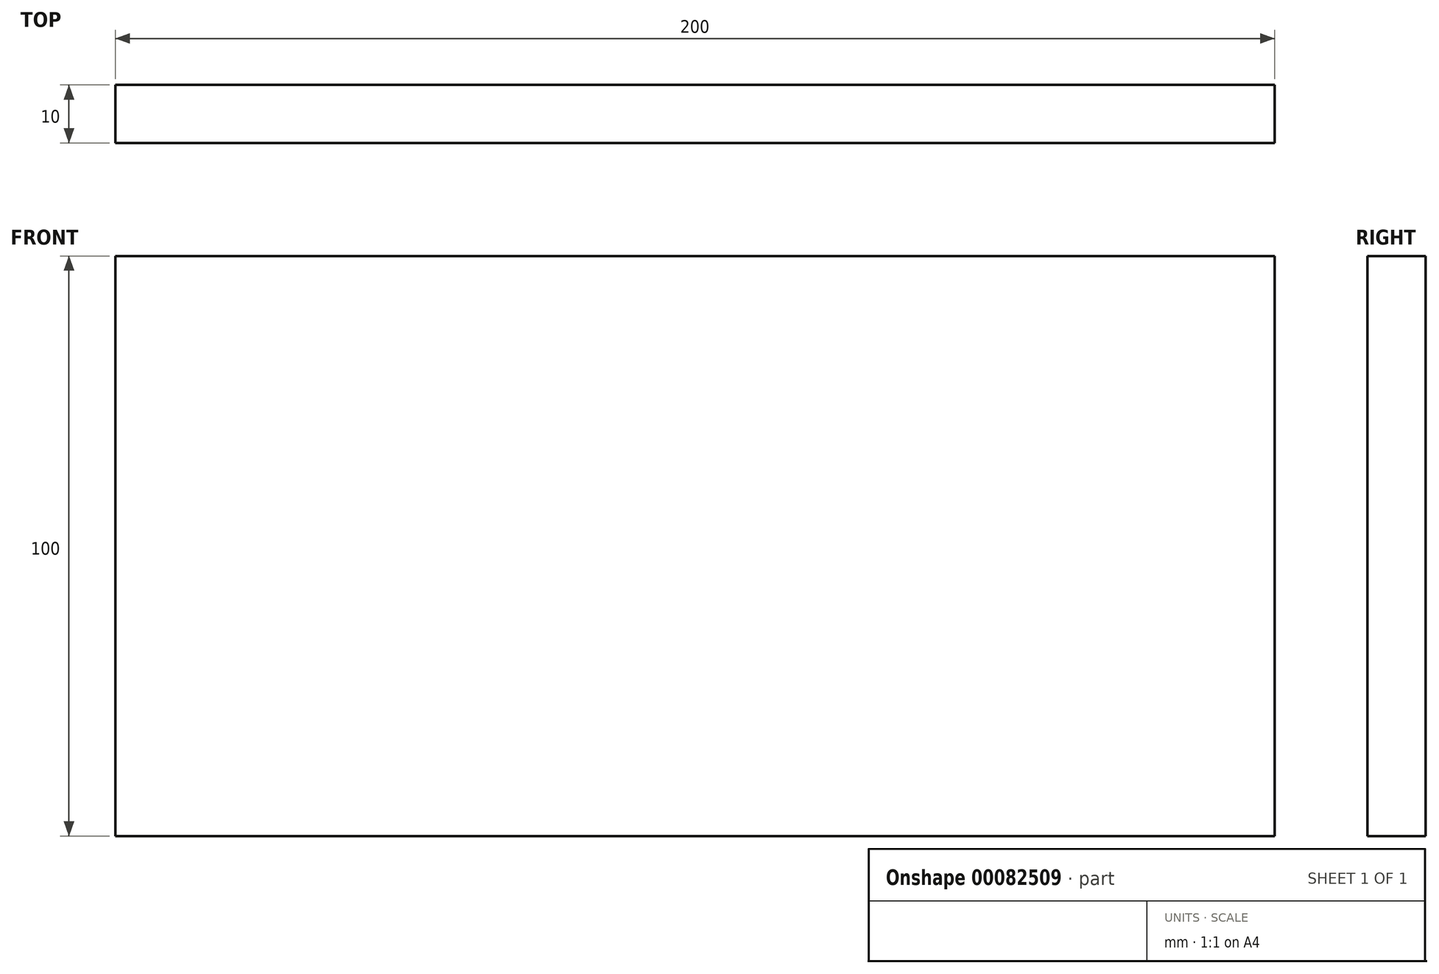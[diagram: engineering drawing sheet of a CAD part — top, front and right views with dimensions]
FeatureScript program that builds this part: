
annotation { "Feature Type Name" : "Feature", "Feature Type Description" : "" }
export const myFeature = defineFeature(function(context is Context, id is Id, definition is map)
    precondition{}
    {
        {
            var Q0;
            Q0=qCreatedBy(makeId("Front.planeOp"),FACE);
            var sketch = newSketch(context, id + "F0", { "sketchPlane" : qUnion([Q0])});
            skLineSegment(sketch, "E0.bottom", {"start": v(0, 0) * mm, "end": v(-200, 0) * mm});
            skLineSegment(sketch, "E0.top", {"start": v(0, 100) * mm, "end": v(-200, 100) * mm});
            skLineSegment(sketch, "E0.left", {"start": v(0, 0) * mm, "end": v(0, 100) * mm});
            skLineSegment(sketch, "E0.right", {"start": v(-200, 0) * mm, "end": v(-200, 100) * mm});
            skSolve(sketch);
        }
        {
            var Q0;
            Q0=qSketchRegion(id+"F0",true);
            extrude(context, id + "F1", {"entities" : qUnion([Q0]), "depth" : 10 * mm});
        }
    });
